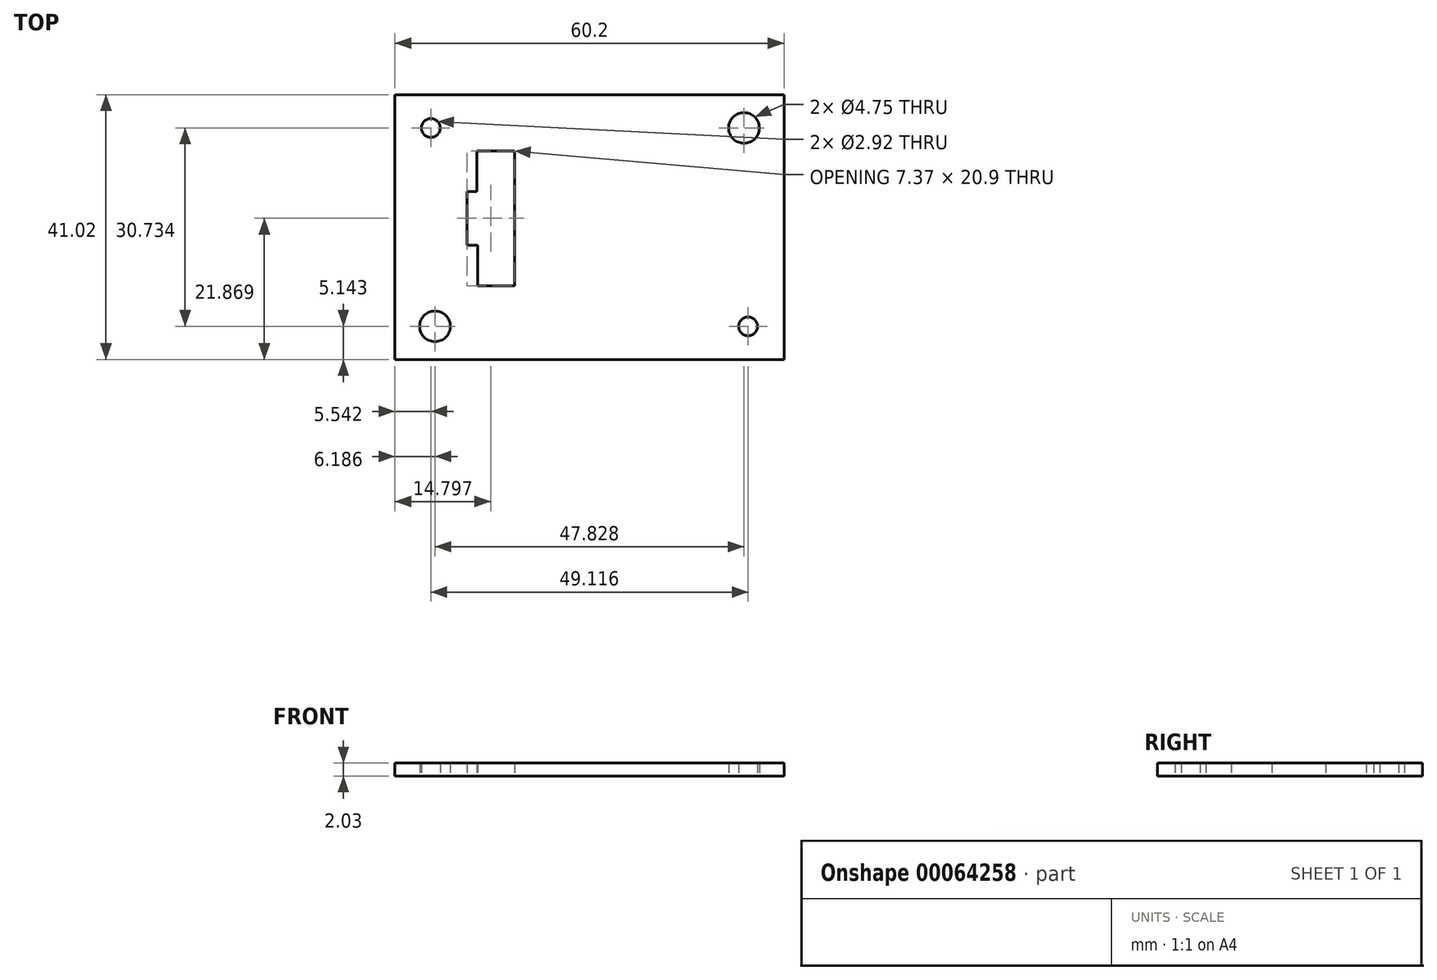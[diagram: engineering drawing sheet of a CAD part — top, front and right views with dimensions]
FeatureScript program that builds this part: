
annotation { "Feature Type Name" : "Feature", "Feature Type Description" : "" }
export const myFeature = defineFeature(function(context is Context, id is Id, definition is map)
    precondition{}
    {
        {
            var Q0;
            Q0=qCreatedBy(makeId("Top.planeOp"),FACE);
            var sketch = newSketch(context, id + "F0", { "sketchPlane" : qUnion([Q0])});
            skLineSegment(sketch, "E0.bottom", {"start": v(19.24, -13.08) * mm, "end": v(-19.24, -13.08) * mm});
            skLineSegment(sketch, "E0.top", {"start": v(19.24, 13.08) * mm, "end": v(-19.24, 13.08) * mm});
            skLineSegment(sketch, "E0.left", {"start": v(19.24, -13.08) * mm, "end": v(19.24, 13.08) * mm});
            skLineSegment(sketch, "E0.right", {"start": v(-19.24, -13.08) * mm, "end": v(-19.24, 13.08) * mm});
            skPoint(sketch, "E0.middle", {"position": v(0, 0) * mm});
            skSolve(sketch);
        }
        {
            var Q0;
            Q0=qCreatedBy(makeId("Top.planeOp"),FACE);
            var sketch = newSketch(context, id + "F1", { "sketchPlane" : qUnion([Q0])});
            skLineSegment(sketch, "E1.bottom", {"start": v(21.53, -15.37) * mm, "end": v(-21.53, -15.37) * mm});
            skLineSegment(sketch, "E1.top", {"start": v(21.53, 15.37) * mm, "end": v(-21.53, 15.37) * mm});
            skLineSegment(sketch, "E1.left", {"start": v(21.53, -15.37) * mm, "end": v(21.53, 15.37) * mm});
            skLineSegment(sketch, "E1.right", {"start": v(-21.53, -15.37) * mm, "end": v(-21.53, 15.37) * mm});
            skPoint(sketch, "E1.middle", {"position": v(0, 0) * mm});
            skSolve(sketch);
        }
        {
            var Q0;
            Q0=qCreatedBy(makeId("Top.planeOp"),FACE);
            var sketch = newSketch(context, id + "F2", { "sketchPlane" : qUnion([Q0])});
            skCircle(sketch, "E2.cCircle", {"center": v(-24.56, 15.37) * mm, "radius": 2.6 * mm, "construction": true});
            skLineSegment(sketch, "E2.0", {"start": v(-23.06, 12.76) * mm, "end": v(-26.06, 12.76) * mm});
            skLineSegment(sketch, "E2.1", {"start": v(-26.06, 12.76) * mm, "end": v(-27.56, 15.37) * mm});
            skLineSegment(sketch, "E2.2", {"start": v(-27.56, 15.37) * mm, "end": v(-26.06, 17.97) * mm});
            skLineSegment(sketch, "E2.3", {"start": v(-26.06, 17.97) * mm, "end": v(-23.06, 17.97) * mm});
            skLineSegment(sketch, "E2.4", {"start": v(-23.06, 17.97) * mm, "end": v(-21.55, 15.37) * mm});
            skLineSegment(sketch, "E2.5", {"start": v(-21.55, 15.37) * mm, "end": v(-23.06, 12.76) * mm});
            skPoint(sketch, "E2.0.midPoint", {"position": v(-24.56, 12.76) * mm});
            skSolve(sketch);
        }
        {
            var Q0;
            Q0=makeQuery(id+"F1.imprint","IMPRINT",FACE,{"disambiguationData":[TD([[makeQuery(id+"F1.imprint","IMPRINT",EDGE,{"derivedFrom":sQuery(id+"F1.wireOp",EDGE,"E1.bottom")}),-1.0]])]});
            var sketch = newSketch(context, id + "F3", { "sketchPlane" : qUnion([Q0])});
            skCircle(sketch, "E3", {"center": v(-24.56, 15.37) * mm, "radius": 1.46 * mm});
            skSolve(sketch);
        }
        {
            var Q0;
            Q0=makeQuery(id+"F1.imprint","IMPRINT",FACE,{"disambiguationData":[TD([[makeQuery(id+"F1.imprint","IMPRINT",EDGE,{"derivedFrom":sQuery(id+"F1.wireOp",EDGE,"E1.bottom")}),-1.0]])]});
            var sketch = newSketch(context, id + "F4", { "sketchPlane" : qUnion([Q0])});
            skCircle(sketch, "E4.cCircle", {"center": v(24.56, -15.37) * mm, "radius": 2.6 * mm, "construction": true});
            skLineSegment(sketch, "E4.0", {"start": v(26.06, -17.97) * mm, "end": v(23.06, -17.97) * mm});
            skLineSegment(sketch, "E4.1", {"start": v(23.06, -17.97) * mm, "end": v(21.55, -15.37) * mm});
            skLineSegment(sketch, "E4.2", {"start": v(21.55, -15.37) * mm, "end": v(23.06, -12.76) * mm});
            skLineSegment(sketch, "E4.3", {"start": v(23.06, -12.76) * mm, "end": v(26.06, -12.76) * mm});
            skLineSegment(sketch, "E4.4", {"start": v(26.06, -12.76) * mm, "end": v(27.56, -15.37) * mm});
            skLineSegment(sketch, "E4.5", {"start": v(27.56, -15.37) * mm, "end": v(26.06, -17.97) * mm});
            skPoint(sketch, "E4.0.midPoint", {"position": v(24.56, -17.97) * mm});
            skSolve(sketch);
        }
        {
            var Q0;
            Q0=makeQuery(id+"F1.imprint","IMPRINT",FACE,{"disambiguationData":[TD([[makeQuery(id+"F1.imprint","IMPRINT",EDGE,{"derivedFrom":sQuery(id+"F1.wireOp",EDGE,"E1.bottom")}),-1.0]])]});
            var sketch = newSketch(context, id + "F5", { "sketchPlane" : qUnion([Q0])});
            skCircle(sketch, "E5", {"center": v(24.56, -15.37) * mm, "radius": 1.46 * mm});
            skSolve(sketch);
        }
        {
            var Q0;
            Q0=makeQuery(id+"F1.imprint","IMPRINT",FACE,{"disambiguationData":[TD([[makeQuery(id+"F1.imprint","IMPRINT",EDGE,{"derivedFrom":sQuery(id+"F1.wireOp",EDGE,"E1.bottom")}),-1.0]])]});
            var sketch = newSketch(context, id + "F6", { "sketchPlane" : qUnion([Q0])});
            skCircle(sketch, "E6", {"center": v(-23.91, -15.37) * mm, "radius": 2.37 * mm});
            skLineSegment(sketch, "E7", {"start": v(-23.91, -15.37) * mm, "end": v(-21.53, -15.37) * mm, "construction": true});
            skSolve(sketch);
        }
        {
            var Q0;
            Q0=makeQuery(id+"F1.imprint","IMPRINT",FACE,{"disambiguationData":[TD([[makeQuery(id+"F1.imprint","IMPRINT",EDGE,{"derivedFrom":sQuery(id+"F1.wireOp",EDGE,"E1.bottom")}),-1.0]])]});
            var sketch = newSketch(context, id + "F7", { "sketchPlane" : qUnion([Q0])});
            skCircle(sketch, "E8", {"center": v(23.91, 15.37) * mm, "radius": 2.37 * mm});
            skLineSegment(sketch, "E9", {"start": v(23.91, 15.37) * mm, "end": v(21.53, 15.37) * mm, "construction": true});
            skSolve(sketch);
        }
        {
            var Q0;
            Q0=qCreatedBy(makeId("Top.planeOp"),FACE);
            var sketch = newSketch(context, id + "F8", { "sketchPlane" : qUnion([Q0])});
            skLineSegment(sketch, "E10.bottom", {"start": v(30.1, -20.51) * mm, "end": v(-30.1, -20.51) * mm});
            skLineSegment(sketch, "E10.top", {"start": v(30.1, 20.51) * mm, "end": v(-30.1, 20.51) * mm});
            skLineSegment(sketch, "E10.left", {"start": v(30.1, -20.51) * mm, "end": v(30.1, 20.51) * mm});
            skLineSegment(sketch, "E10.right", {"start": v(-30.1, -20.51) * mm, "end": v(-30.1, 20.51) * mm});
            skPoint(sketch, "E10.middle", {"position": v(0, 0) * mm});
            skSolve(sketch);
        }
        {
            var Q0;
            Q0=qSketchRegion(id+"F8",true);
            extrude(context, id + "F9", {"entities" : qUnion([Q0]), "depth" : 2.03 * mm, "hasOffset" : true, "offsetDistance" : 2.3 * mm});
        }
        {
            var Q0;
            Q0=qSketchRegion(id+"F6",true);
            var Q1;
            Q1=qSketchRegion(id+"F7",true);
            extrude(context, id + "F10", {"entities" : qUnion([Q0, Q1]), "operationType" : NewBodyOperationType.REMOVE, "depth" : 12.2 * mm, "offsetDistance" : 25.4 * mm});
        }
        {
            var Q0;
            Q0=qSketchRegion(id+"F3",true);
            var Q1;
            Q1=qSketchRegion(id+"F5",true);
            extrude(context, id + "F11", {"entities" : qUnion([Q0, Q1]), "operationType" : NewBodyOperationType.REMOVE, "depth" : 12.2 * mm, "offsetDistance" : 25.4 * mm});
        }
        {
            var Q0;
            Q0=qCreatedBy(makeId("Top.planeOp"),FACE);
            var sketch = newSketch(context, id + "F12", { "sketchPlane" : qUnion([Q0])});
            skLineSegment(sketch, "E11", {"start": v(-11.62, 11.81) * mm, "end": v(-11.62, -9.1) * mm});
            skLineSegment(sketch, "E12", {"start": v(-17.34, -9.1) * mm, "end": v(-11.62, -9.1) * mm});
            skLineSegment(sketch, "E13", {"start": v(-11.62, 11.81) * mm, "end": v(-17.46, 11.81) * mm});
            skLineSegment(sketch, "E14", {"start": v(-17.34, -9.1) * mm, "end": v(-17.34, -2.8) * mm});
            skLineSegment(sketch, "E15", {"start": v(-17.46, 5.52) * mm, "end": v(-17.46, 11.81) * mm});
            skLineSegment(sketch, "E16", {"start": v(-18.99, -2.8) * mm, "end": v(-17.34, -2.8) * mm});
            skLineSegment(sketch, "E17", {"start": v(-17.46, 5.52) * mm, "end": v(-18.99, 5.52) * mm});
            skLineSegment(sketch, "E18", {"start": v(-18.99, -2.8) * mm, "end": v(-18.99, 5.52) * mm});
            skSolve(sketch);
        }
        {
            var Q0;
            Q0 = qSketchRegion(id + "F12", true);
            extrude(context, id + "F13", {"entities" : qUnion([Q0]), "operationType" : NewBodyOperationType.REMOVE, "depth" : 2.3 * mm, "offsetDistance" : 25.4 * mm});
        }
    });
